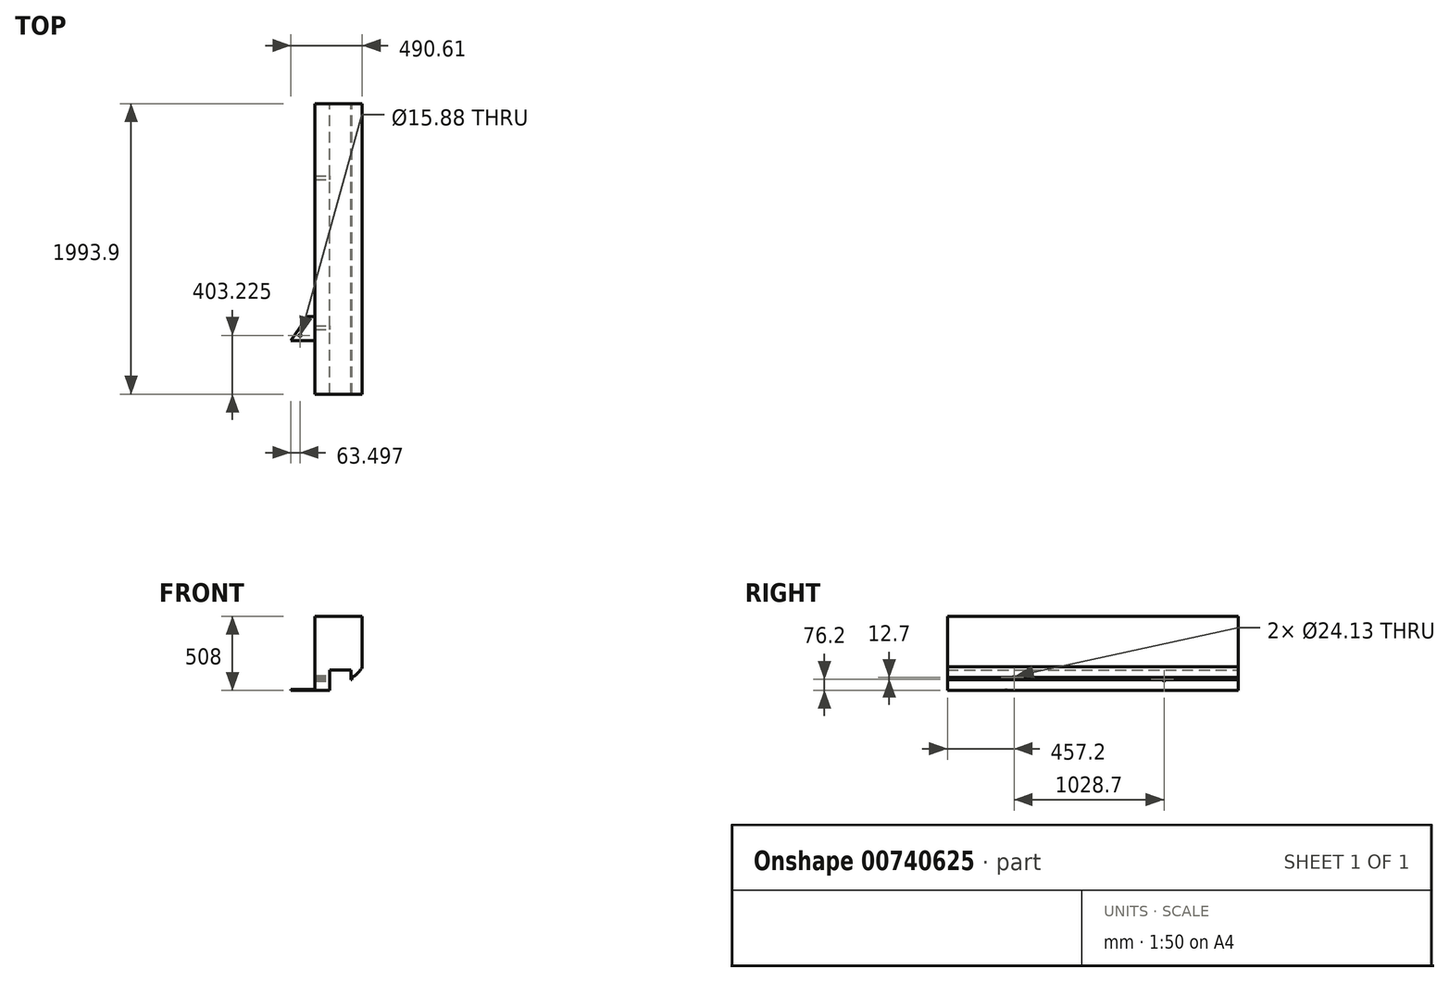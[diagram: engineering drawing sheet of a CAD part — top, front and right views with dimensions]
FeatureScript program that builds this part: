
annotation { "Feature Type Name" : "Feature", "Feature Type Description" : "" }
export const myFeature = defineFeature(function(context is Context, id is Id, definition is map)
    precondition{}
    {
        {
            var Q0;
            Q0=qCreatedBy(makeId("Front.planeOp"),FACE);
            var sketch = newSketch(context, id + "F0", { "sketchPlane" : qUnion([Q0])});
            skLineSegment(sketch, "E0", {"start": v(0, 0) * mm, "end": v(-101.27, 0) * mm});
            skLineSegment(sketch, "E1", {"start": v(0, 0) * mm, "end": v(0, 139.7) * mm});
            skLineSegment(sketch, "E2", {"start": v(0, 139.7) * mm, "end": v(146.05, 139.7) * mm});
            skLineSegment(sketch, "E3", {"start": v(146.05, 139.7) * mm, "end": v(146.05, 73.03) * mm});
            skLineSegment(sketch, "E4", {"start": v(146.05, 73.03) * mm, "end": v(152.4, 73.03) * mm});
            skLineSegment(sketch, "E5", {"start": v(152.4, 73.03) * mm, "end": v(152.4, 89.54) * mm});
            skLineSegment(sketch, "E6", {"start": v(152.4, 89.54) * mm, "end": v(152.4, 161.38) * mm, "construction": true});
            skLineSegment(sketch, "E7", {"start": v(152.4, 161.38) * mm, "end": v(224.24, 161.38) * mm, "construction": true});
            skArc(sketch, "E8", {"start": v(152.4, 89.53) * mm, "mid": v(194.28, 119.5) * mm, "end": v(224.24, 161.38) * mm});
            skLineSegment(sketch, "E9", {"start": v(152.4, 89.53) * mm, "end": v(224.24, 161.38) * mm, "construction": true});
            skLineSegment(sketch, "E10", {"start": v(-101.27, 0) * mm, "end": v(-101.27, 508) * mm});
            skLineSegment(sketch, "E11", {"start": v(-101.27, 508) * mm, "end": v(224.24, 508) * mm});
            skLineSegment(sketch, "E12", {"start": v(224.24, 508) * mm, "end": v(224.24, 161.38) * mm});
            skSolve(sketch);
        }
        {
            var Q0;
            Q0=makeQuery(id+"F0.imprint","IMPRINT",FACE,{"disambiguationData":[TD([[makeQuery(id+"F0.imprint","IMPRINT",EDGE,{"derivedFrom":sQuery(id+"F0.wireOp",EDGE,"E0")}),-1.0]])]});
            extrude(context, id + "F1", {"entities" : qUnion([Q0]), "depth" : 1993.9 * mm, "offsetDistance" : 25.4 * mm});
        }
        {
            var Q0;
            Q0=makeQuery(id+"F1.opExtrude","SWEPT_FACE",FACE,{"disambiguationData":[OSD([sQuery(id+"F0.wireOp",EDGE,"E1")])]});
            var sketch = newSketch(context, id + "F2", { "sketchPlane" : qUnion([Q0])});
            skCircle(sketch, "E13", {"center": v(-1536.7, 88.9) * mm, "radius": 12.07 * mm});
            skCircle(sketch, "E14", {"center": v(-508, 76.2) * mm, "radius": 12.07 * mm});
            skSolve(sketch);
        }
        {
            var Q0;
            Q0=makeQuery(id+"F2.imprint","IMPRINT",FACE,{"disambiguationData":[TD([[makeQuery(id+"F2.imprint","IMPRINT",EDGE,{"derivedFrom":sQuery(id+"F2.wireOp",EDGE,"E13")}),1.0]])]});
            var Q1;
            Q1=makeQuery(id+"F2.imprint","IMPRINT",FACE,{"disambiguationData":[TD([[makeQuery(id+"F2.imprint","IMPRINT",EDGE,{"derivedFrom":sQuery(id+"F2.wireOp",EDGE,"E14")}),1.0]])]});
            extrude(context, id + "F3", {"entities" : qUnion([Q0, Q1]), "operationType" : NewBodyOperationType.REMOVE, "oppositeDirection" : true, "depth" : 254 * mm, "offsetDistance" : 25.4 * mm});
        }
        {
            var Q0;
            Q0=makeQuery(id+"F1.opExtrude","SWEPT_FACE",FACE,{"disambiguationData":[OSD([sQuery(id+"F0.wireOp",EDGE,"E0")])]});
            var sketch = newSketch(context, id + "F4", { "sketchPlane" : qUnion([Q0])});
            skLineSegment(sketch, "E15.0", {"start": v(0, 1548.77) * mm, "end": v(0, 1524.64) * mm});
            skLineSegment(sketch, "E16", {"start": v(-101.27, 1625.6) * mm, "end": v(-266.37, 1625.6) * mm});
            skLineSegment(sketch, "E17", {"start": v(-101.27, 1460.5) * mm, "end": v(-101.27, 1625.6) * mm});
            skCircle(sketch, "E18", {"center": v(-202.87, 1590.67) * mm, "radius": 7.94 * mm});
            skLineSegment(sketch, "E19", {"start": v(-101.27, 1460.5) * mm, "end": v(-151.58, 1460.5) * mm});
            skLineSegment(sketch, "E20", {"start": v(-151.58, 1460.5) * mm, "end": v(-266.37, 1625.6) * mm});
            skSolve(sketch);
        }
        {
            var Q0;
            Q0=makeQuery(id+"F4.imprint","IMPRINT",FACE,{"disambiguationData":[TD([[makeQuery(id+"F4.imprint","IMPRINT",EDGE,{"derivedFrom":sQuery(id+"F4.wireOp",EDGE,"E16")}),1.0]])]});
            extrude(context, id + "F5", {"entities" : qUnion([Q0]), "operationType" : NewBodyOperationType.ADD, "oppositeDirection" : true, "depth" : 6.35 * mm, "offsetDistance" : 25.4 * mm});
        }
    });
